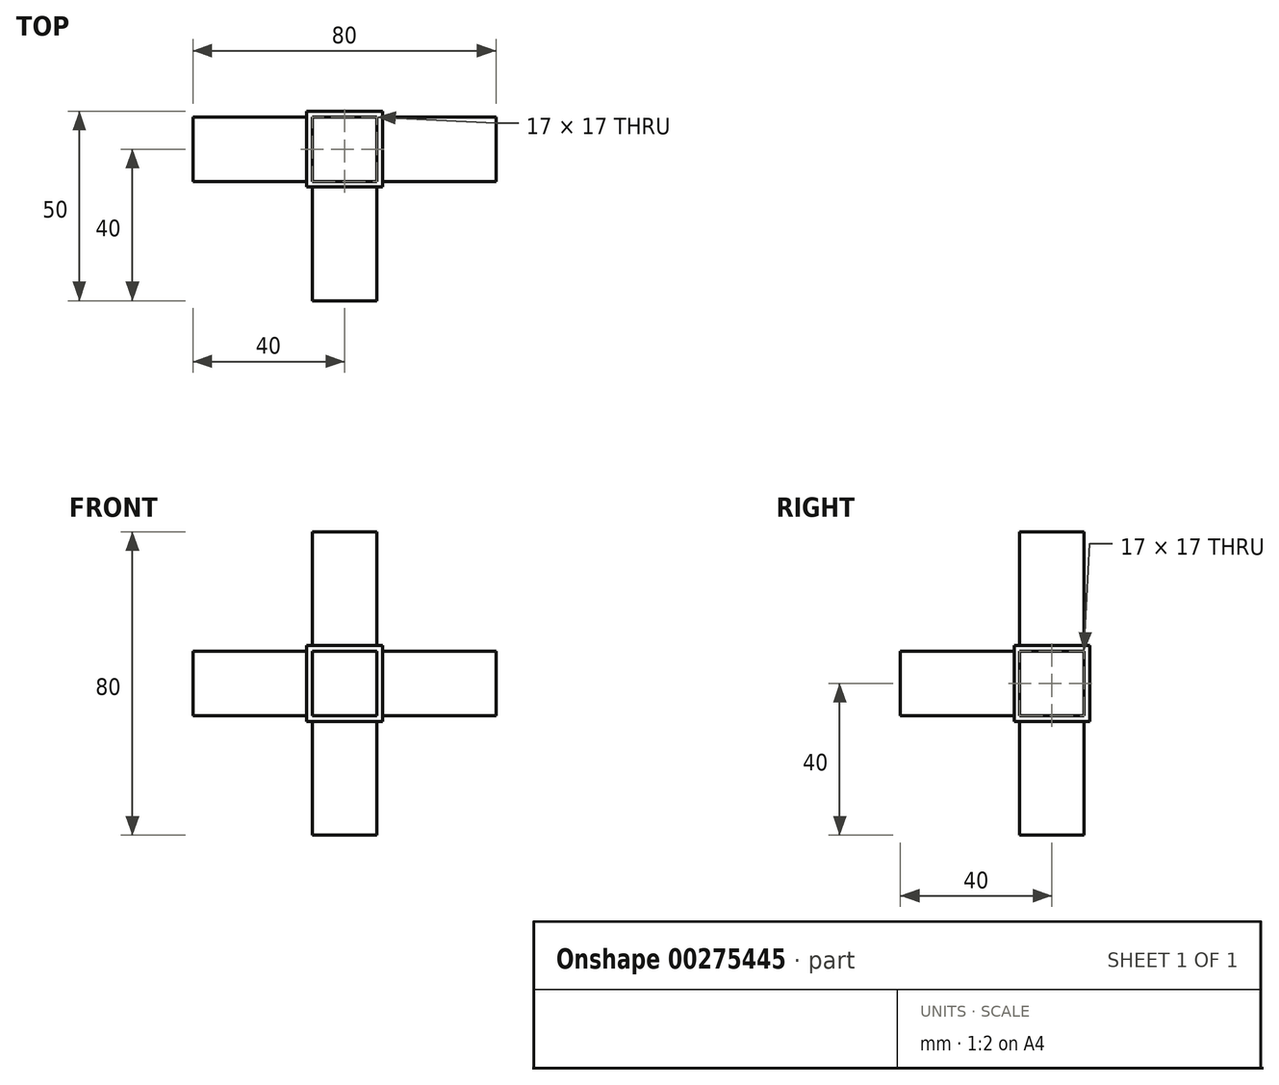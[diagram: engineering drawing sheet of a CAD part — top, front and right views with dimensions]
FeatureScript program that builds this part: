
annotation { "Feature Type Name" : "Feature", "Feature Type Description" : "" }
export const myFeature = defineFeature(function(context is Context, id is Id, definition is map)
    precondition{}
    {
        {
            var Q0;
            Q0=qCreatedBy(makeId("Top.planeOp"),FACE);
            var sketch = newSketch(context, id + "F0", { "sketchPlane" : qUnion([Q0])});
            skLineSegment(sketch, "E0.bottom", {"start": v(10, -10) * mm, "end": v(-10, -10) * mm});
            skLineSegment(sketch, "E0.top", {"start": v(10, 10) * mm, "end": v(-10, 10) * mm});
            skLineSegment(sketch, "E0.left", {"start": v(10, -10) * mm, "end": v(10, 10) * mm});
            skLineSegment(sketch, "E0.right", {"start": v(-10, -10) * mm, "end": v(-10, 10) * mm});
            skPoint(sketch, "E0.middle", {"position": v(0, 0) * mm});
            skLineSegment(sketch, "E1", {"start": v(0, -10) * mm, "end": v(8.5, -10) * mm});
            skLineSegment(sketch, "E2.bottom", {"start": v(8.5, -10) * mm, "end": v(-8.5, -10) * mm});
            skLineSegment(sketch, "E2.top", {"start": v(8.5, -40) * mm, "end": v(-8.5, -40) * mm});
            skLineSegment(sketch, "E2.left", {"start": v(8.5, -10) * mm, "end": v(8.5, -40) * mm});
            skLineSegment(sketch, "E2.right", {"start": v(-8.5, -10) * mm, "end": v(-8.5, -40) * mm});
            skLineSegment(sketch, "E3", {"start": v(-10, 0) * mm, "end": v(-10, -8.5) * mm});
            skLineSegment(sketch, "E4.bottom", {"start": v(-10, -8.5) * mm, "end": v(-40, -8.5) * mm});
            skLineSegment(sketch, "E4.top", {"start": v(-10, 8.5) * mm, "end": v(-40, 8.5) * mm});
            skLineSegment(sketch, "E4.left", {"start": v(-10, -8.5) * mm, "end": v(-10, 8.5) * mm});
            skLineSegment(sketch, "E4.right", {"start": v(-40, -8.5) * mm, "end": v(-40, 8.5) * mm});
            skSolve(sketch);
        }
        {
            var Q0;
            {var subQ1=sQuery(id+"F0.wireOp",EDGE,"E0.top");Q0=makeQuery(id+"F0.imprint","IMPRINT",FACE,{"disambiguationData":[TD([[makeQuery(id+"F0.imprint","IMPRINT",EDGE,{"derivedFrom":subQ1}),1.0]])]});}
            extrude(context, id + "F1", {"entities" : qUnion([Q0]), "depth" : 20 * mm});
        }
        {
            var Q0;
            {var subQ4=sQuery(id+"F0.wireOp",EDGE,"E4.bottom");Q0=makeQuery(id+"F0.imprint","IMPRINT",FACE,{"disambiguationData":[TD([[makeQuery(id+"F0.imprint","IMPRINT",EDGE,{"derivedFrom":subQ4}),-1.0]])]});}
            var Q1;
            Q1=makeQuery(id+"F0.imprint","IMPRINT",FACE,{"disambiguationData":[TD([[makeQuery(id+"F0.imprint","IMPRINT",EDGE,{"derivedFrom":sQuery(id+"F0.wireOp",EDGE,"E2.top")}),-1.0]])]});
            extrude(context, id + "F2", {"entities" : qUnion([Q0, Q1]), "operationType" : NewBodyOperationType.ADD, "depth" : 18.5 * mm, "hasSecondDirection" : true, "secondDirectionOppositeDirection" : false, "secondDirectionDepth" : 1.5 * mm});
        }
        {
            var Q0;
            Q0=makeQuery(id+"F1.opExtrude","CAP_FACE",FACE,{"disambiguationData":[OSD([sQuery(id+"F0.wireOp",EDGE,"E0.bottom"),sQuery(id+"F0.wireOp",EDGE,"E0.top"),sQuery(id+"F0.wireOp",EDGE,"E0.left"),sQuery(id+"F0.wireOp",EDGE,"E0.right"),sQuery(id+"F0.wireOp",EDGE,"E2.bottom"),sQuery(id+"F0.wireOp",EDGE,"E4.left")])],"isStart":false});
            var sketch = newSketch(context, id + "F3", { "sketchPlane" : qUnion([Q0])});
            skLineSegment(sketch, "E5.bottom", {"start": v(8.5, -8.5) * mm, "end": v(-8.5, -8.5) * mm});
            skLineSegment(sketch, "E5.top", {"start": v(8.5, 8.5) * mm, "end": v(-8.5, 8.5) * mm});
            skLineSegment(sketch, "E5.left", {"start": v(8.5, -8.5) * mm, "end": v(8.5, 8.5) * mm});
            skLineSegment(sketch, "E5.right", {"start": v(-8.5, -8.5) * mm, "end": v(-8.5, 8.5) * mm});
            skPoint(sketch, "E5.middle", {"position": v(0, 0) * mm});
            skSolve(sketch);
        }
        {
            var Q0;
            Q0=qSketchRegion(id+"F3",true);
            extrude(context, id + "F4", {"entities" : qUnion([Q0]), "operationType" : NewBodyOperationType.ADD, "depth" : 30 * mm});
        }
        {
            var Q0;
            Q0=makeQuery(id+"F1.opExtrude","CAP_FACE",FACE,{"disambiguationData":[OSD([sQuery(id+"F0.wireOp",EDGE,"E0.bottom"),sQuery(id+"F0.wireOp",EDGE,"E0.top"),sQuery(id+"F0.wireOp",EDGE,"E0.left"),sQuery(id+"F0.wireOp",EDGE,"E0.right"),sQuery(id+"F0.wireOp",EDGE,"E2.bottom"),sQuery(id+"F0.wireOp",EDGE,"E4.left")])],"isStart":true});
            var sketch = newSketch(context, id + "F5", { "sketchPlane" : qUnion([Q0])});
            skLineSegment(sketch, "E6.bottom", {"start": v(8.5, -8.5) * mm, "end": v(-8.5, -8.5) * mm});
            skLineSegment(sketch, "E6.top", {"start": v(8.5, 8.5) * mm, "end": v(-8.5, 8.5) * mm});
            skLineSegment(sketch, "E6.left", {"start": v(8.5, -8.5) * mm, "end": v(8.5, 8.5) * mm});
            skLineSegment(sketch, "E6.right", {"start": v(-8.5, -8.5) * mm, "end": v(-8.5, 8.5) * mm});
            skPoint(sketch, "E6.middle", {"position": v(0, 0) * mm});
            skSolve(sketch);
        }
        {
            var Q0;
            Q0=qSketchRegion(id+"F5",true);
            extrude(context, id + "F6", {"entities" : qUnion([Q0]), "operationType" : NewBodyOperationType.ADD, "depth" : 30 * mm});
        }
        {
            var Q0;
            Q0=makeQuery(id+"F1.opExtrude","SWEPT_FACE",FACE,{"disambiguationData":[OSD([sQuery(id+"F0.wireOp",EDGE,"E0.left")])]});
            var sketch = newSketch(context, id + "F7", { "sketchPlane" : qUnion([Q0])});
            skLineSegment(sketch, "E7.bottom", {"start": v(8.5, 1.5) * mm, "end": v(-8.5, 1.5) * mm});
            skLineSegment(sketch, "E7.top", {"start": v(8.5, 18.5) * mm, "end": v(-8.5, 18.5) * mm});
            skLineSegment(sketch, "E7.left", {"start": v(8.5, 1.5) * mm, "end": v(8.5, 18.5) * mm});
            skLineSegment(sketch, "E7.right", {"start": v(-8.5, 1.5) * mm, "end": v(-8.5, 18.5) * mm});
            skPoint(sketch, "E7.middle", {"position": v(0, 10) * mm});
            skPoint(sketch, "E7.middle.positionSnap0", {"position": v(10, 10) * mm});
            skPoint(sketch, "E7.middle.positionSnap1", {"position": v(0, 20) * mm});
            skPoint(sketch, "E7.centerSnap0", {"position": v(10, 10) * mm});
            skPoint(sketch, "E7.centerSnap1", {"position": v(0, 20) * mm});
            skSolve(sketch);
        }
        {
            var Q0;
            Q0 = qSketchRegion(id + "F7", true);
            extrude(context, id + "F8", {"entities" : qUnion([Q0]), "operationType" : NewBodyOperationType.ADD, "depth" : 30 * mm});
        }
    });
